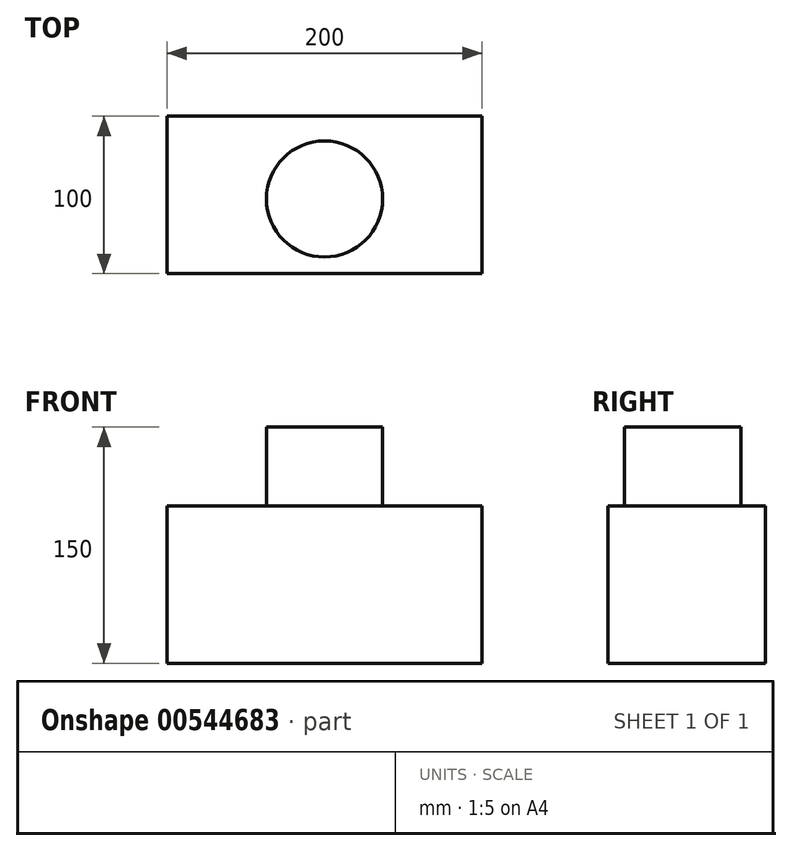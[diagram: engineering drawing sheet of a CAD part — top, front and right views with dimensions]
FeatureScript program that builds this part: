
annotation { "Feature Type Name" : "Feature", "Feature Type Description" : "" }
export const myFeature = defineFeature(function(context is Context, id is Id, definition is map)
    precondition{}
    {
        {
            var Q0;
            Q0=qCreatedBy(makeId("Front.planeOp"),FACE);
            var sketch = newSketch(context, id + "F0", { "sketchPlane" : qUnion([Q0])});
            skLineSegment(sketch, "E0.bottom", {"start": v(100, -50) * mm, "end": v(-100, -50) * mm});
            skLineSegment(sketch, "E0.top", {"start": v(100, 50) * mm, "end": v(-100, 50) * mm});
            skLineSegment(sketch, "E0.left", {"start": v(100, -50) * mm, "end": v(100, 50) * mm});
            skLineSegment(sketch, "E0.right", {"start": v(-100, -50) * mm, "end": v(-100, 50) * mm});
            skPoint(sketch, "E0.middle", {"position": v(0, 0) * mm});
            skSolve(sketch);
        }
        {
            var Q0;
            Q0=makeQuery(id+"F0.imprint","IMPRINT",FACE,{"disambiguationData":[TD([[makeQuery(id+"F0.imprint","IMPRINT",EDGE,{"derivedFrom":sQuery(id+"F0.wireOp",EDGE,"E0.bottom")}),-1.0]])]});
            extrude(context, id + "F1", {"entities" : qUnion([Q0]), "oppositeDirection" : true, "depth" : 100 * mm, "offsetDistance" : 25 * mm});
        }
        {
            var Q0;
            Q0=makeQuery(id+"F1.opExtrude","SWEPT_FACE",FACE,{"disambiguationData":[OSD([sQuery(id+"F0.wireOp",EDGE,"E0.top")])]});
            var sketch = newSketch(context, id + "F2", { "sketchPlane" : qUnion([Q0])});
            skCircle(sketch, "E1", {"center": v(0, 47.45) * mm, "radius": 36.89 * mm});
            skSolve(sketch);
        }
        {
            var Q0;
            Q0=makeQuery(id+"F2.imprint","IMPRINT",FACE,{"disambiguationData":[TD([[makeQuery(id+"F2.imprint","IMPRINT",EDGE,{"derivedFrom":sQuery(id+"F2.wireOp",EDGE,"E1")}),1.0]])]});
            extrude(context, id + "F3", {"entities" : qUnion([Q0]), "operationType" : NewBodyOperationType.ADD, "depth" : 50 * mm, "offsetDistance" : 25 * mm});
        }
    });
